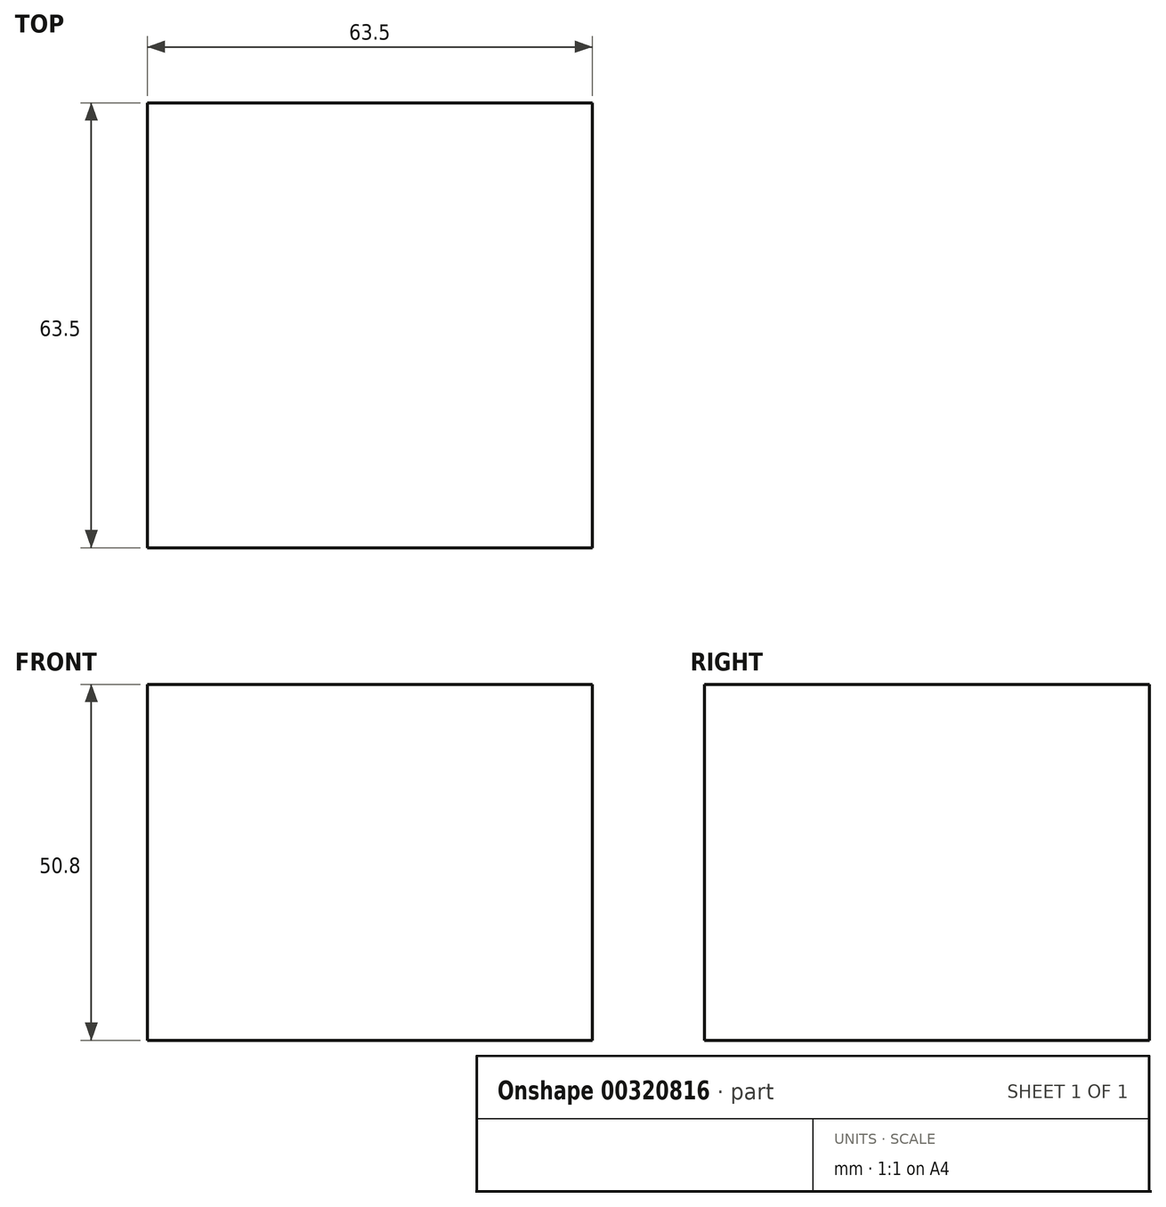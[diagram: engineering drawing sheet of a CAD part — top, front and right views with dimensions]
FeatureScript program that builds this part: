
annotation { "Feature Type Name" : "Feature", "Feature Type Description" : "" }
export const myFeature = defineFeature(function(context is Context, id is Id, definition is map)
    precondition{}
    {
        {
            var Q0;
            Q0=qCreatedBy(makeId("Top.planeOp"),FACE);
            var sketch = newSketch(context, id + "F0", { "sketchPlane" : qUnion([Q0])});
            skLineSegment(sketch, "E0", {"start": v(-32.06, 20.77) * mm, "end": v(31.44, 20.77) * mm});
            skLineSegment(sketch, "E1", {"start": v(31.44, 20.77) * mm, "end": v(31.44, -42.73) * mm});
            skLineSegment(sketch, "E2", {"start": v(31.44, -42.73) * mm, "end": v(-32.06, -42.73) * mm});
            skLineSegment(sketch, "E3", {"start": v(-32.06, -42.73) * mm, "end": v(-32.06, 20.77) * mm});
            skSolve(sketch);
        }
        {
            var Q0;
            Q0=makeQuery(id+"F0.imprint","IMPRINT",FACE,{"disambiguationData":[TD([[makeQuery(id+"F0.imprint","IMPRINT",EDGE,{"derivedFrom":sQuery(id+"F0.wireOp",EDGE,"E0")}),-1.0]])]});
            extrude(context, id + "F1", {"entities" : qUnion([Q0]), "depth" : 50.8 * mm});
        }
    });
